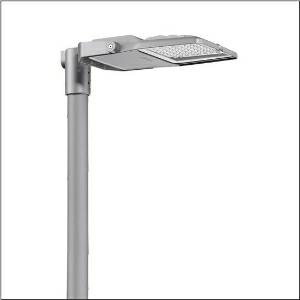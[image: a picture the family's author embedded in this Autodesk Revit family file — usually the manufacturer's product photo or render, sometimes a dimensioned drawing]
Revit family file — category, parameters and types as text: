
# Revit family: floodlight_fl_21_mini___pl33t_5xa7775c2f3a_8bfe
name_source: partatom
category: Lighting Fixtures
units: mm (PartAtom-declared; Revit-internal decimal feet)

## family parameters
Cut with Voids When Loaded = No
Host = Face
Light Source = No
Part Type = Normal
Room Calculation Point = No
Round Connector Dimension = Use Diameter
Shared = No

## types (1)
- --- (1 x LED, 12050 lm, 89 W, 3000K)
    Apparent Load = 89 VA
    CIE Flux Codes = 26 75 99 100 100
    Color Rendering = 70
    Color Temperature = 3000K
    Default Elevation = 1800 mm
    Description = Floodlight FL 21 mini, floodlight, primary light control with lens, of PMMA, primary optical cover: protective disc, of toughened safety glass, transparent, light distribution: PL33T, light emission: direct distribution, installation type: surface-mounted, LED, High Power LED, rated luminous flux: 12.050lm, luminous efficacy: 135lm/W, light colour: 730, colour temperature: 3000K, control gear: ECG Smart Interface, control: flexible luminous flux parameterisation, time-dependent luminous flux control, constant luminous flux control, overheat protection, presetting dimming logarithmic, with terminal, 6-pole, mains connection: 220..240V, AC, 50/60Hz, start of lifetime: 89W, end of lifetime: 94W, reduction: 43W, luminaire housing, of diecast aluminium, powder-coated, Siteco® metallic grey (DB 702S), corrosivity category C5 according to DIN EN ISO 12944, mast bracket, of steel, galvanised, powder-coated, Siteco® metallic grey (DB 702S), protection rating (complete): IP66, insulation class (complete): insulation class II (safety insulation), certification: CE, ENEC, VDE, protection symbol: D, impact resistance: IK08, permissible operating ambient temperature: -40..+40°C, permissible operating ambient temperature for outdoor applications: -40..+50°C, standard: DIN EN 12944, packaging unit: 1 piece

Light Distribution: PL33T
    Height = 70 mm
    Lamp = 1 x LED
    Lamp Light Flux = 12050 lm
    Lamp Power = 89 W
    Lamp count = 1
    Length = 485 mm
    Luminous efficacy = 135 lm/W
    Manufacturer = Siteco
    ModVariant = No
    Model = 5XA7775C2F3A
    Number of Poles = 1
    OnlyDefault = Yes
    Power Factor = 1
    Product Name = Floodlight FL 21 mini | PL33T
    Product group = floodlight | pylon top
    ProductGroupID = 6101
    Protection Class = Protection class II
    Protection Degree = IP 66
    RLX_Detail_Level = 1
    RlxData = <blob elided: 100637 chars, md5=dec7032e>
    Socket = socket
    Standby Power = 0 W
    System Light Flux = 12050 lm
    System Power = 89 W
    Type Comments = factory setting: luminous flux: 100 % | dim-lin: 254 | 456 mA
    Type Image = l_1007125.jpg
    URL = http://relux.com
    VarID = @adj_058631
    Voltage = 0 V
    Weight = 0.00 kg
    Width = 337 mm

## geometry (parser evidence)
native form markers: Blend x4, Sweep x12
no freeform markers — native parametric forms only
